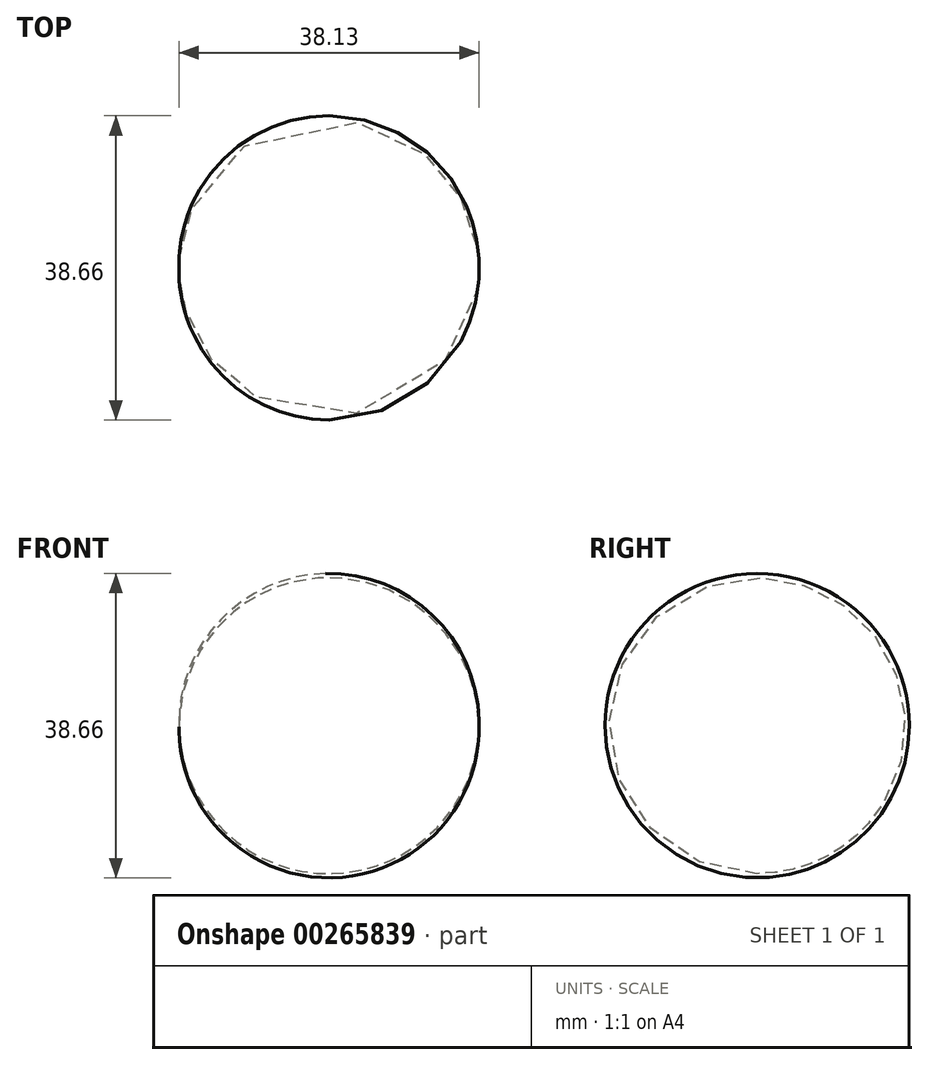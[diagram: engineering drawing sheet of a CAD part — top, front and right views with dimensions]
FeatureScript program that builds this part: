
annotation { "Feature Type Name" : "Feature", "Feature Type Description" : "" }
export const myFeature = defineFeature(function(context is Context, id is Id, definition is map)
    precondition{}
    {
        {
            var Q0;
            Q0=qCreatedBy(makeId("Front.planeOp"),FACE);
            var sketch = newSketch(context, id + "F0", { "sketchPlane" : qUnion([Q0])});
            skArc(sketch, "E0", {"start": v(58.24, 44.46) * mm, "mid": v(38.77, 63.37) * mm, "end": v(20.13, 43.64) * mm});
            skLineSegment(sketch, "E1", {"start": v(20.13, 43.64) * mm, "end": v(58.24, 44.46) * mm});
            skSolve(sketch);
        }
        {
            var Q0;
            Q0=makeQuery(id+"F0.imprint","IMPRINT",FACE,{"disambiguationData":[TD([[makeQuery(id+"F0.imprint","IMPRINT",EDGE,{"derivedFrom":sQuery(id+"F0.wireOp",EDGE,"E0")}),1.0]])]});
            var Q1;
            Q1=sQuery(id+"F0.wireOp",EDGE,"E1");
            revolve(context, id + "F1", {"entities" : qUnion([Q0]), "axis" : qUnion([Q1]), "revolveType" : RevolveType.FULL});
        }
    });
